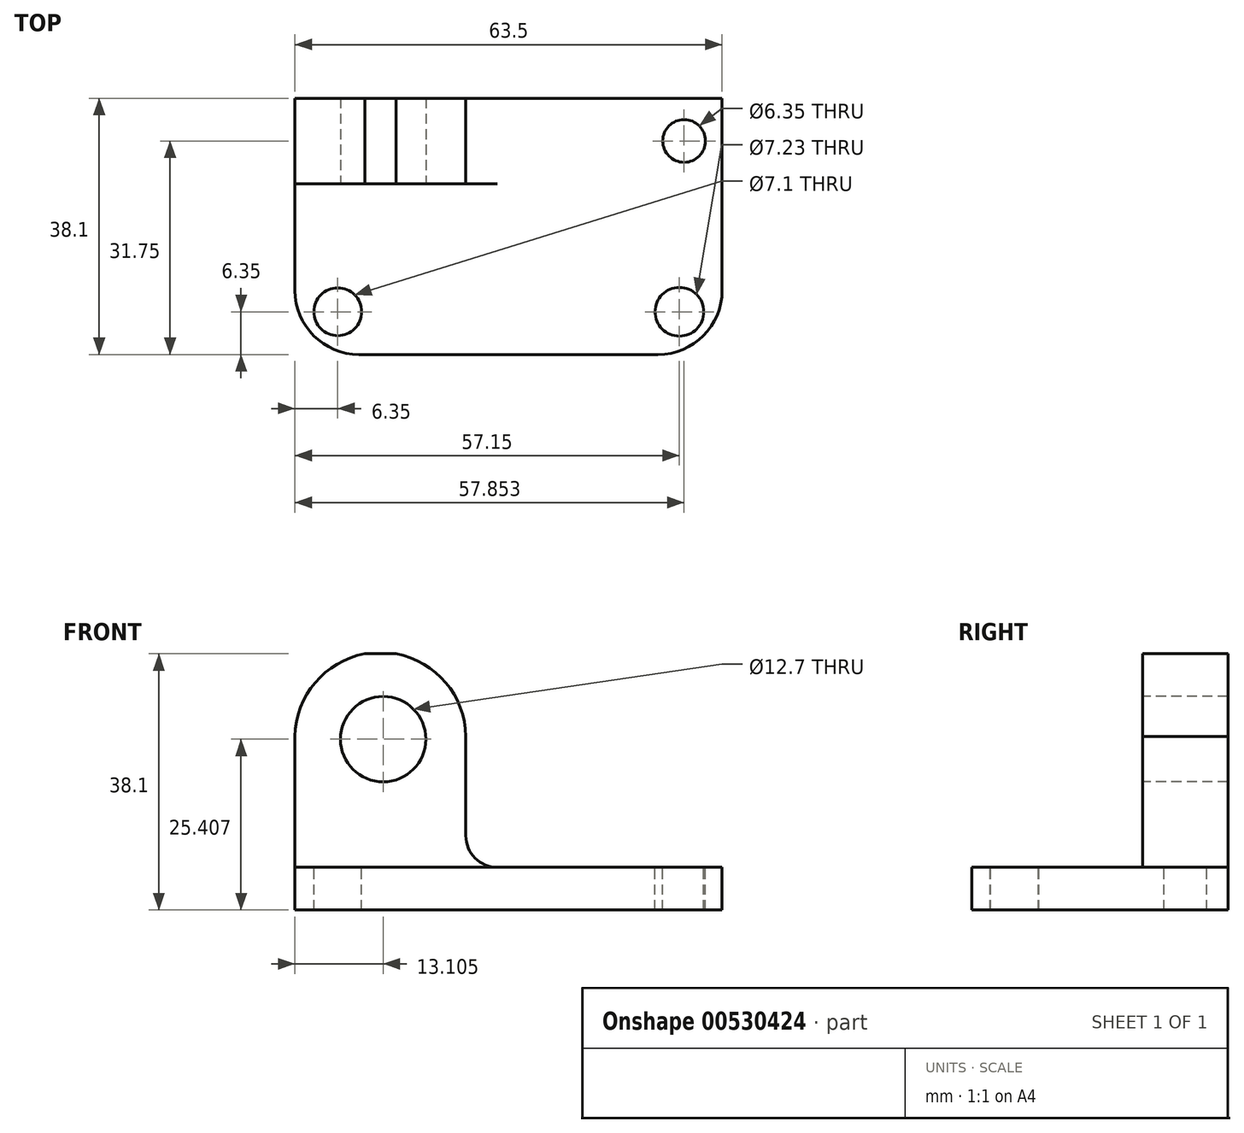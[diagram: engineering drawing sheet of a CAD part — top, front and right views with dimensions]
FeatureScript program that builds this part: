
annotation { "Feature Type Name" : "Feature", "Feature Type Description" : "" }
export const myFeature = defineFeature(function(context is Context, id is Id, definition is map)
    precondition{}
    {
        {
            var Q0;
            Q0=qCreatedBy(makeId("Top.planeOp"),FACE);
            var sketch = newSketch(context, id + "F0", { "sketchPlane" : qUnion([Q0])});
            skLineSegment(sketch, "E0.bottom", {"start": v(0, 38.1) * mm, "end": v(63.5, 38.1) * mm});
            skLineSegment(sketch, "E0.top", {"start": v(0, 0) * mm, "end": v(63.5, 0) * mm});
            skLineSegment(sketch, "E0.left", {"start": v(0, 38.1) * mm, "end": v(0, 0) * mm});
            skLineSegment(sketch, "E0.right", {"start": v(63.5, 38.1) * mm, "end": v(63.5, 0) * mm});
            skSolve(sketch);
        }
        {
            var Q0;
            Q0=makeQuery(id+"F0.imprint","IMPRINT",FACE,{"disambiguationData":[TD([[makeQuery(id+"F0.imprint","IMPRINT",EDGE,{"derivedFrom":sQuery(id+"F0.wireOp",EDGE,"E0.bottom")}),-1.0]])]});
            extrude(context, id + "F1", {"entities" : qUnion([Q0]), "depth" : 6.35 * mm, "offsetDistance" : 25.4 * mm});
        }
        {
            var Q0;
            Q0=makeQuery(id+"F1.opExtrude","CAP_FACE",FACE,{"disambiguationData":[OSD([sQuery(id+"F0.wireOp",EDGE,"E0.bottom"),sQuery(id+"F0.wireOp",EDGE,"E0.top"),sQuery(id+"F0.wireOp",EDGE,"E0.left"),sQuery(id+"F0.wireOp",EDGE,"E0.right")])],"isStart":false});
            var sketch = newSketch(context, id + "F2", { "sketchPlane" : qUnion([Q0])});
            skCircle(sketch, "E1", {"center": v(6.35, 6.35) * mm, "radius": 3.55 * mm});
            skCircle(sketch, "E2", {"center": v(57.85, 31.75) * mm, "radius": 3.18 * mm});
            skCircle(sketch, "E3", {"center": v(57.15, 6.35) * mm, "radius": 3.62 * mm});
            skSolve(sketch);
        }
        {
            var Q0;
            Q0=makeQuery(id+"F2.imprint","IMPRINT",FACE,{"disambiguationData":[TD([[makeQuery(id+"F2.imprint","IMPRINT",EDGE,{"derivedFrom":sQuery(id+"F2.wireOp",EDGE,"E1")}),1.0]])]});
            var Q1;
            Q1=makeQuery(id+"F2.imprint","IMPRINT",FACE,{"disambiguationData":[TD([[makeQuery(id+"F2.imprint","IMPRINT",EDGE,{"derivedFrom":sQuery(id+"F2.wireOp",EDGE,"E3")}),1.0]])]});
            var Q2;
            Q2=makeQuery(id+"F2.imprint","IMPRINT",FACE,{"disambiguationData":[TD([[makeQuery(id+"F2.imprint","IMPRINT",EDGE,{"derivedFrom":sQuery(id+"F2.wireOp",EDGE,"E2")}),1.0]])]});
            extrude(context, id + "F3", {"entities" : qUnion([Q0, Q1, Q2]), "operationType" : NewBodyOperationType.REMOVE, "oppositeDirection" : true, "depth" : 25.4 * mm, "offsetDistance" : 25.4 * mm});
        }
        {
            var Q0;
            Q0=makeQuery(id+"F1.opExtrude","CAP_FACE",FACE,{"disambiguationData":[OSD([sQuery(id+"F0.wireOp",EDGE,"E0.bottom"),sQuery(id+"F0.wireOp",EDGE,"E0.top"),sQuery(id+"F0.wireOp",EDGE,"E0.left"),sQuery(id+"F0.wireOp",EDGE,"E0.right")])],"isStart":false});
            var sketch = newSketch(context, id + "F4", { "sketchPlane" : qUnion([Q0])});
            skLineSegment(sketch, "E4", {"start": v(0, 25.4) * mm, "end": v(25.4, 25.4) * mm});
            skLineSegment(sketch, "E5", {"start": v(25.4, 25.4) * mm, "end": v(25.4, 38.1) * mm});
            skSolve(sketch);
        }
        {
            var Q0;
            {var subQ0=sQuery(id+"F4.wireOp",EDGE,"E4");Q0=makeQuery(id+"F4.imprint","IMPRINT",FACE,{"disambiguationData":[TD([[makeQuery(id+"F4.imprint","IMPRINT",EDGE,{"derivedFrom":subQ0}),1.0]])]});}
            extrude(context, id + "F5", {"entities" : qUnion([Q0]), "operationType" : NewBodyOperationType.ADD, "depth" : 31.75 * mm, "offsetDistance" : 25.4 * mm});
        }
        {
            var Q0;
            Q0=makeQuery(id+"F5.opExtrude","SWEPT_FACE",FACE,{"disambiguationData":[OSD([sQuery(id+"F4.wireOp",EDGE,"E4")])]});
            var sketch = newSketch(context, id + "F6", { "sketchPlane" : qUnion([Q0])});
            skCircle(sketch, "E6", {"center": v(13.1, 25.4) * mm, "radius": 6.35 * mm});
            skArc(sketch, "E7", {"start": v(25.4, 25.4) * mm, "mid": v(12.7, 38.32) * mm, "end": v(0, 25.4) * mm});
            skSolve(sketch);
        }
        {
            var Q0;
            Q0=makeQuery(id+"F6.imprint","IMPRINT",FACE,{"disambiguationData":[TD([[makeQuery(id+"F6.imprint","IMPRINT",EDGE,{"derivedFrom":sQuery(id+"F6.wireOp",EDGE,"E6")}),1.0]])]});
            var Q1;
            {var subQ0=sQuery(id+"F6.wireOp",EDGE,"E7");var subQ1=sQuery(id+"F4.wireOp",EDGE,"E4");var subQ2=makeQuery(id+"F5.opExtrude","CAP_EDGE",EDGE,{"disambiguationData":[OSD([subQ1])],"isStart":false});var subQ3=makeQuery(id+"F6.imprint","INTERSECT",VERTEX,{"disambiguationData":[OD(1.0)],"derivedFrom":[subQ2,subQ0]});Q1=makeQuery(id+"F6.imprint","IMPRINT",FACE,{"disambiguationData":[TD([[makeQuery(id+"F6.imprint","IMPRINT",EDGE,{"disambiguationData":[TD([[subQ3,-1.0]])],"derivedFrom":subQ0}),-1.0]])]});}
            var Q2;
            {var subQ0=sQuery(id+"F6.wireOp",EDGE,"E7");var subQ1=sQuery(id+"F4.wireOp",EDGE,"E4");var subQ4=makeQuery(id+"F5.opExtrude","CAP_EDGE",EDGE,{"disambiguationData":[OSD([subQ1])],"isStart":false});var subQ5=makeQuery(id+"F6.imprint","INTERSECT",VERTEX,{"disambiguationData":[OD(0.0)],"derivedFrom":[subQ4,subQ0]});Q2=makeQuery(id+"F6.imprint","IMPRINT",FACE,{"disambiguationData":[TD([[makeQuery(id+"F6.imprint","IMPRINT",EDGE,{"disambiguationData":[TD([[subQ5,1.0]])],"derivedFrom":subQ0}),-1.0]])]});}
            extrude(context, id + "F7", {"entities" : qUnion([Q0, Q1, Q2]), "operationType" : NewBodyOperationType.REMOVE, "endBound" : BoundingType.THROUGH_ALL, "oppositeDirection" : true, "depth" : 25.4 * mm, "offsetDistance" : 25.4 * mm});
        }
        {
            var Q0;
            Q0=makeQuery(id+"F1.opExtrude","SWEPT_EDGE",EDGE,{"disambiguationData":[OSD([sQuery(id+"F0.wireOp",EDGE,"E0.top"),sQuery(id+"F0.wireOp",EDGE,"E0.left")])]});
            var Q1;
            Q1=makeQuery(id+"F1.opExtrude","SWEPT_EDGE",EDGE,{"disambiguationData":[OSD([sQuery(id+"F0.wireOp",EDGE,"E0.top"),sQuery(id+"F0.wireOp",EDGE,"E0.right")])]});
            fillet(context, id + "F8", {"entities" : qUnion([Q0, Q1]), "radius" : 9.52 * mm, "tangentPropagation" : true, "allowEdgeOverflow" : false});
        }
        {
            var Q0;
            Q0=makeQuery(id+"F5.opExtrude","SWEPT_FACE",FACE,{"disambiguationData":[OSD([sQuery(id+"F4.wireOp",EDGE,"E5")])]});
            var sketch = newSketch(context, id + "F9", { "sketchPlane" : qUnion([Q0])});
            skLineSegment(sketch, "E8.bottom", {"start": v(25.4, 16.09) * mm, "end": v(38.1, 16.09) * mm});
            skLineSegment(sketch, "E8.top", {"start": v(25.4, 6.35) * mm, "end": v(38.1, 6.35) * mm});
            skLineSegment(sketch, "E8.left", {"start": v(25.4, 16.09) * mm, "end": v(25.4, 6.35) * mm});
            skLineSegment(sketch, "E8.right", {"start": v(38.1, 16.09) * mm, "end": v(38.1, 6.35) * mm});
            skSolve(sketch);
        }
        {
            var Q0;
            Q0=makeQuery(id+"F9.imprint","IMPRINT",FACE,{"disambiguationData":[TD([[makeQuery(id+"F9.imprint","IMPRINT",EDGE,{"derivedFrom":sQuery(id+"F9.wireOp",EDGE,"E8.bottom")}),-1.0]])]});
            extrude(context, id + "F10", {"entities" : qUnion([Q0]), "operationType" : NewBodyOperationType.ADD, "depth" : 12.7 * mm, "offsetDistance" : 25.4 * mm});
        }
        {
            var Q0;
            Q0=makeQuery(id+"F10.boolean.opBoolean","MERGE",FACE,{"derivedFrom":[makeQuery(id+"F5.opExtrude","SWEPT_FACE",FACE,{"disambiguationData":[OSD([sQuery(id+"F4.wireOp",EDGE,"E4")])]}),makeQuery(id+"F10.opExtrude","SWEPT_FACE",FACE,{"disambiguationData":[OSD([sQuery(id+"F9.wireOp",EDGE,"E8.left")])]})]});
            var sketch = newSketch(context, id + "F11", { "sketchPlane" : qUnion([Q0])});
            skLineSegment(sketch, "E9", {"start": v(25.4, 16.09) * mm, "end": v(25.4, 6.35) * mm});
            skCircle(sketch, "E10", {"center": v(30.1, 11.04) * mm, "radius": 4.7 * mm});
            skSolve(sketch);
        }
        {
            var Q0;
            {var subQ0=sQuery(id+"F11.wireOp",EDGE,"E10");var subQ1=makeQuery(id+"F11.imprint","INTERSECT",VERTEX,{"derivedFrom":[sQuery(id+"F11.wireOp",EDGE,"E9"),subQ0]});Q0=makeQuery(id+"F11.imprint","IMPRINT",FACE,{"disambiguationData":[TD([[makeQuery(id+"F11.imprint","IMPRINT",EDGE,{"disambiguationData":[TD([[subQ1,-1.0]])],"derivedFrom":subQ0}),1.0]])]});}
            var Q1;
            {var subQ0=sQuery(id+"F9.wireOp",EDGE,"E8.left");var subQ9=makeQuery(id+"F10.opExtrude","CAP_EDGE",EDGE,{"disambiguationData":[OSD([subQ0])],"isStart":false});Q1=makeQuery(id+"F11.imprint","IMPRINT",FACE,{"disambiguationData":[TD([[makeQuery(id+"F11.imprint","IMPRINT",EDGE,{"derivedFrom":subQ9}),-1.0]])]});}
            extrude(context, id + "F12", {"entities" : qUnion([Q0, Q1]), "operationType" : NewBodyOperationType.REMOVE, "oppositeDirection" : true, "depth" : 25.4 * mm, "offsetDistance" : 25.4 * mm});
        }
    });
